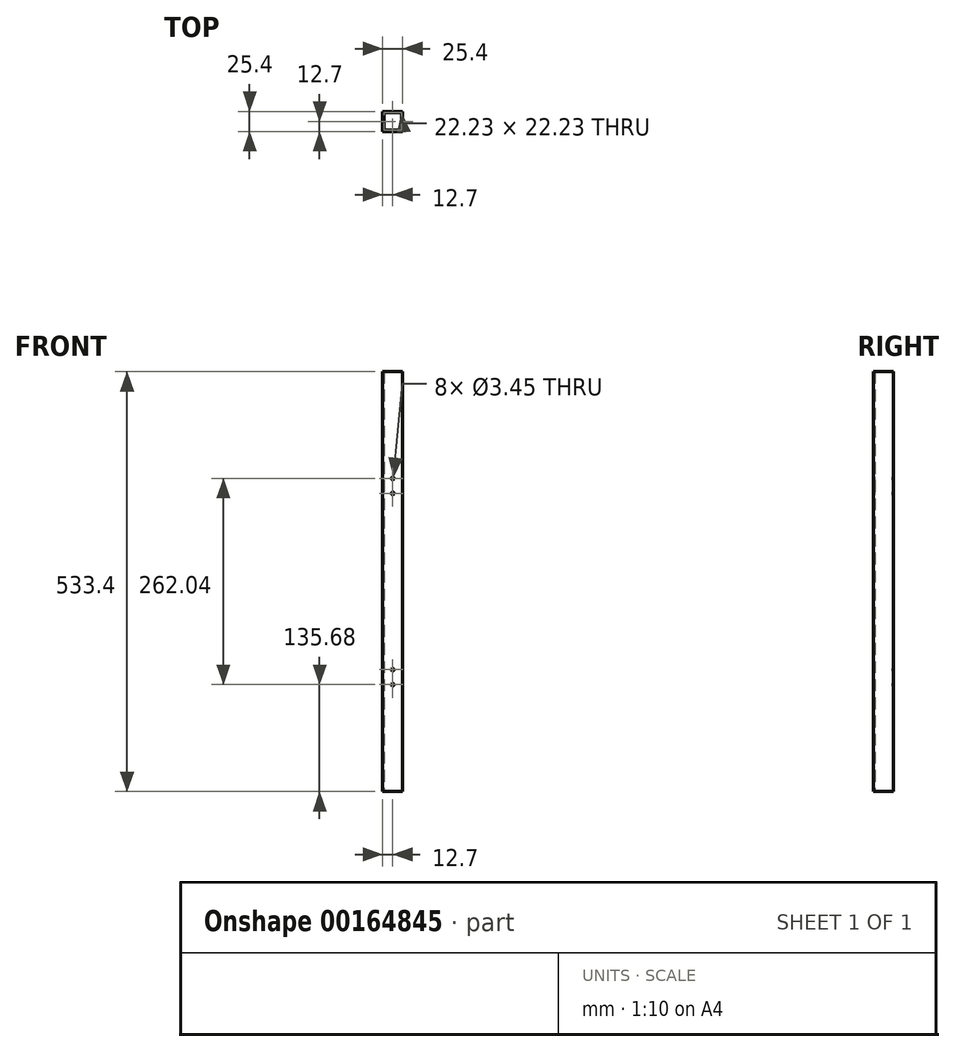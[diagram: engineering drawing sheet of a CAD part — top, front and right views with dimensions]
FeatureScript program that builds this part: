
annotation { "Feature Type Name" : "Feature", "Feature Type Description" : "" }
export const myFeature = defineFeature(function(context is Context, id is Id, definition is map)
    precondition{}
    {
        {
            var Q0;
            Q0=qCreatedBy(makeId("Top.planeOp"),FACE);
            var sketch = newSketch(context, id + "F0", { "sketchPlane" : qUnion([Q0])});
            skLineSegment(sketch, "E0.bottom", {"start": v(11.11, -11.11) * mm, "end": v(-11.11, -11.11) * mm});
            skLineSegment(sketch, "E0.top", {"start": v(11.11, 11.11) * mm, "end": v(-11.11, 11.11) * mm});
            skLineSegment(sketch, "E0.left", {"start": v(11.11, -11.11) * mm, "end": v(11.11, 11.11) * mm});
            skLineSegment(sketch, "E0.right", {"start": v(-11.11, -11.11) * mm, "end": v(-11.11, 11.11) * mm});
            skPoint(sketch, "E0.middle", {"position": v(0, 0) * mm});
            skLineSegment(sketch, "E1.bottom", {"start": v(12.7, -12.7) * mm, "end": v(-12.7, -12.7) * mm});
            skLineSegment(sketch, "E1.top", {"start": v(12.7, 12.7) * mm, "end": v(-12.7, 12.7) * mm});
            skLineSegment(sketch, "E1.left", {"start": v(12.7, -12.7) * mm, "end": v(12.7, 12.7) * mm});
            skLineSegment(sketch, "E1.right", {"start": v(-12.7, -12.7) * mm, "end": v(-12.7, 12.7) * mm});
            skSolve(sketch);
        }
        {
            var Q0;
            Q0=qSketchRegion(id+"F0",true);
            extrude(context, id + "F1", {"entities" : qUnion([Q0]), "depth" : 533.4 * mm});
        }
        {
            var Q0;
            Q0=makeQuery(id+"F1.opExtrude","SWEPT_FACE",FACE,{"disambiguationData":[OSD([sQuery(id+"F0.wireOp",EDGE,"E1.bottom")])]});
            var sketch = newSketch(context, id + "F2", { "sketchPlane" : qUnion([Q0])});
            skLineSegment(sketch, "E2", {"start": v(0, 0) * mm, "end": v(0, 135.68) * mm, "construction": true});
            skLineSegment(sketch, "E3", {"start": v(0, 135.68) * mm, "end": v(0, 154.73) * mm, "construction": true});
            skLineSegment(sketch, "E4", {"start": v(0, 533.4) * mm, "end": v(0, 397.72) * mm, "construction": true});
            skLineSegment(sketch, "E5", {"start": v(0, 397.72) * mm, "end": v(0, 378.67) * mm, "construction": true});
            skCircle(sketch, "E6", {"center": v(0, 135.68) * mm, "radius": 1.73 * mm});
            skCircle(sketch, "E7", {"center": v(0, 154.73) * mm, "radius": 1.73 * mm});
            skCircle(sketch, "E8", {"center": v(0, 397.72) * mm, "radius": 1.73 * mm});
            skCircle(sketch, "E9", {"center": v(0, 378.67) * mm, "radius": 1.73 * mm});
            skSolve(sketch);
        }
        {
            var Q0;
            Q0=qSketchRegion(id+"F2",true);
            var Q1;
            Q1=makeQuery(id+"F1.opExtrude","SWEPT_FACE",FACE,{"disambiguationData":[OSD([sQuery(id+"F0.wireOp",EDGE,"E1.top")])]});
            extrude(context, id + "F3", {"entities" : qUnion([Q0]), "operationType" : NewBodyOperationType.REMOVE, "endBound" : BoundingType.UP_TO_SURFACE, "oppositeDirection" : true, "endBoundEntityFace" : qUnion([Q1]), "depth" : 25.4 * mm});
        }
    });
